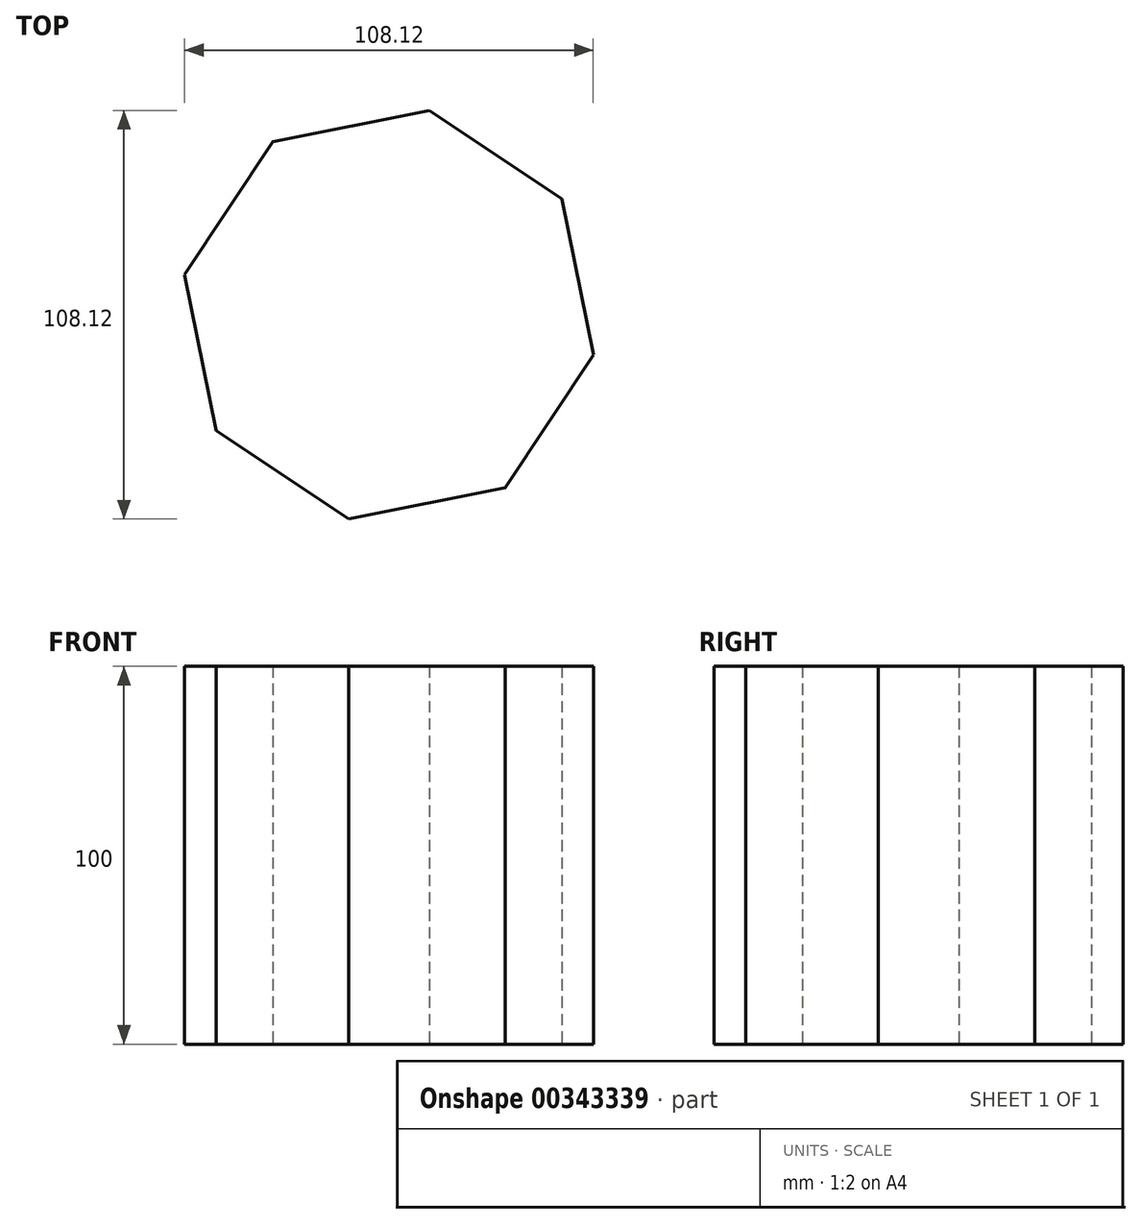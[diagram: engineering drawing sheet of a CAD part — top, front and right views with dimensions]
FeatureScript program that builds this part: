
annotation { "Feature Type Name" : "Feature", "Feature Type Description" : "" }
export const myFeature = defineFeature(function(context is Context, id is Id, definition is map)
    precondition{}
    {
        {
            var Q0;
            Q0=qCreatedBy(makeId("Top.planeOp"),FACE);
            var sketch = newSketch(context, id + "F0", { "sketchPlane" : qUnion([Q0])});
            skCircle(sketch, "E0.cCircle", {"center": v(0, 0) * mm, "radius": 55.1 * mm, "construction": true});
            skLineSegment(sketch, "E0.0", {"start": v(-30.7, 45.76) * mm, "end": v(10.65, 54.06) * mm});
            skLineSegment(sketch, "E0.1", {"start": v(10.65, 54.06) * mm, "end": v(45.76, 30.7) * mm});
            skLineSegment(sketch, "E0.2", {"start": v(45.76, 30.7) * mm, "end": v(54.06, -10.65) * mm});
            skLineSegment(sketch, "E0.3", {"start": v(54.06, -10.65) * mm, "end": v(30.7, -45.76) * mm});
            skLineSegment(sketch, "E0.4", {"start": v(30.7, -45.76) * mm, "end": v(-10.65, -54.06) * mm});
            skLineSegment(sketch, "E0.5", {"start": v(-10.65, -54.06) * mm, "end": v(-45.76, -30.7) * mm});
            skLineSegment(sketch, "E0.6", {"start": v(-45.76, -30.7) * mm, "end": v(-54.06, 10.65) * mm});
            skLineSegment(sketch, "E0.7", {"start": v(-54.06, 10.65) * mm, "end": v(-30.7, 45.76) * mm});
            skSolve(sketch);
        }
        {
            var Q0;
            Q0=makeQuery(id+"F0.imprint","IMPRINT",FACE,{"disambiguationData":[TD([[makeQuery(id+"F0.imprint","IMPRINT",EDGE,{"derivedFrom":sQuery(id+"F0.wireOp",EDGE,"E0.0")}),-1.0]])]});
            extrude(context, id + "F1", {"entities" : qUnion([Q0]), "depth" : 100 * mm});
        }
    });
